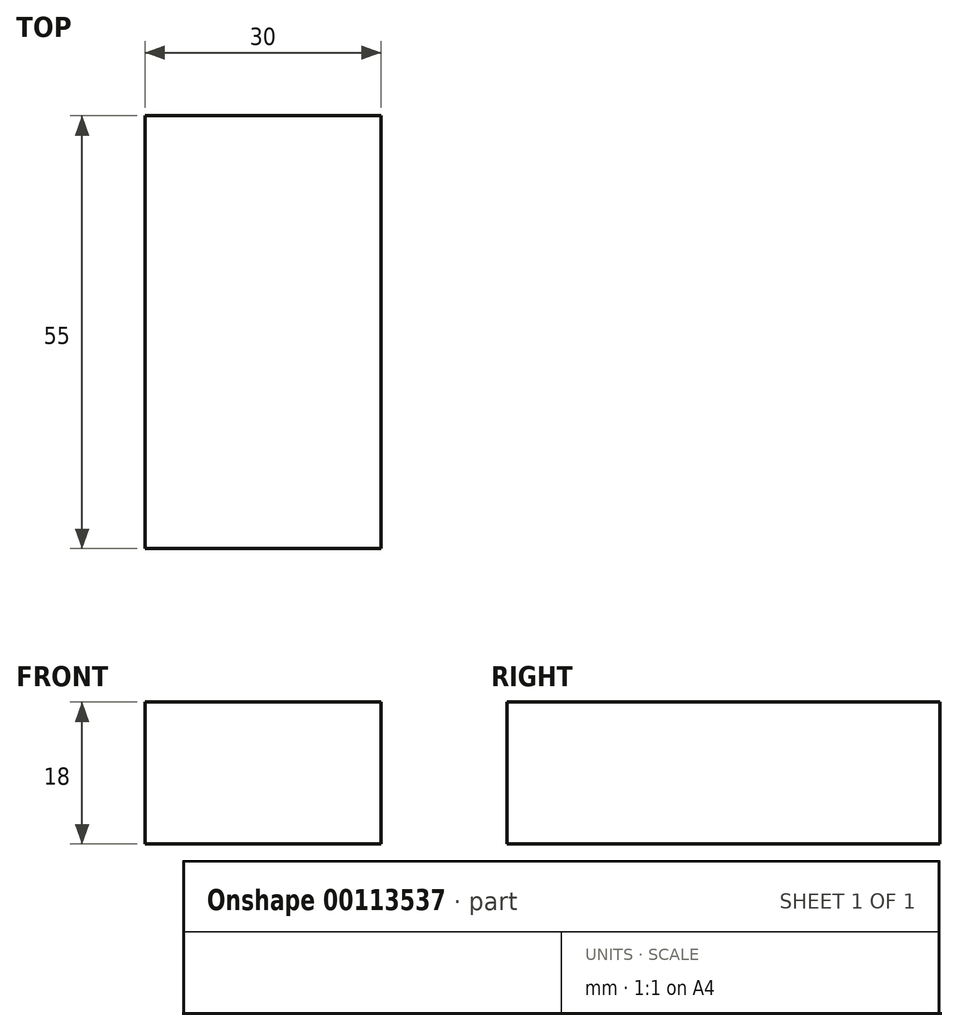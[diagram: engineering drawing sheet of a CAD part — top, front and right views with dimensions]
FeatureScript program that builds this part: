
annotation { "Feature Type Name" : "Feature", "Feature Type Description" : "" }
export const myFeature = defineFeature(function(context is Context, id is Id, definition is map)
    precondition{}
    {
        {
            var Q0;
            Q0=qCreatedBy(makeId("Top.planeOp"),FACE);
            var sketch = newSketch(context, id + "F0", { "sketchPlane" : qUnion([Q0])});
            skLineSegment(sketch, "E0.bottom", {"start": v(15, -27.5) * mm, "end": v(-15, -27.5) * mm});
            skLineSegment(sketch, "E0.top", {"start": v(15, 27.5) * mm, "end": v(-15, 27.5) * mm});
            skLineSegment(sketch, "E0.left", {"start": v(15, -27.5) * mm, "end": v(15, 27.5) * mm});
            skLineSegment(sketch, "E0.right", {"start": v(-15, -27.5) * mm, "end": v(-15, 27.5) * mm});
            skPoint(sketch, "E0.middle", {"position": v(0, 0) * mm});
            skSolve(sketch);
        }
        {
            var Q0;
            Q0=qSketchRegion(id+"F0",true);
            extrude(context, id + "F1", {"entities" : qUnion([Q0]), "depth" : 18 * mm});
        }
    });
